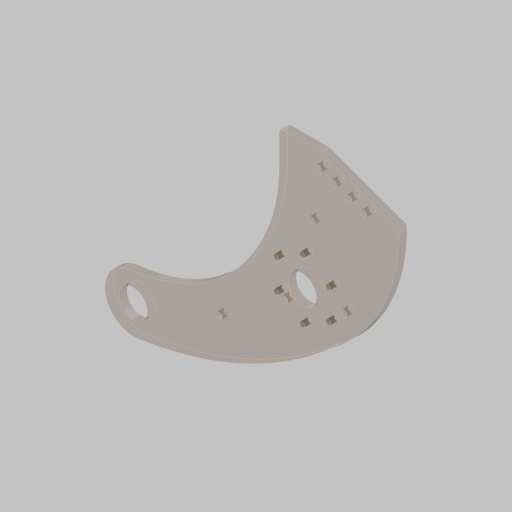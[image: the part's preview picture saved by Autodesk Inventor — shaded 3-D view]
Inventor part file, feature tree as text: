
AUTODESK INVENTOR PART (.ipt)
format: ipt  version: 2023.5 (Build 275446000, 446)  size: 253,440 bytes
history: native  units: in
note: dims shown in document units (in); Inventor stores cm internally (conversion verified against a paired STEP export)
features: sketch x5, hole x4, projected_geometry x3, extrude x2, fillet x2
ambient origin geometry x8: Origin, YZ Plane, XZ Plane, XY Plane, X Axis, Y Axis, Z Axis, Center Point
bodies: Solid1 (feature_tree)
feature tree (16):
  sketch  "Sketch1"  dims[d0=1.0in d1=3.0in]
  extrude  "Extrusion1"  Depth=3.0in
  hole  "Hole1"  [1 undecoded]
  hole  "Hole2"  [1 undecoded]
  fillet  "Fillet1"  Radius=0.5in
  hole  "Hole3"  [1 undecoded]
  hole  "Hole4"  [1 undecoded]
  extrude  "Extrusion2"  Depth=0.25in
  fillet  "Fillet2"  Radius=11.5in
  sketch  "Sketch5"  dims[d8=1.875in d9=0.875in]
  sketch  "Sketch3"  dims[d2=8.75in d3=5.75in]
  projected_geometry  "Projected Loop1"
  sketch  "Sketch4"  dims[d4=1.0in d5=3.0in d7=0.5in]
  projected_geometry  "Projected Loop2"
  sketch  "Sketch6"  dims[d10=1.9685in d12=0.5in d13=0.3937in d15=1.0in d17=0.5in d18=0.375in d19=11.5in d20=0.25in d21=0.0in d22=0.201in d23=0.38in d24=0.385in d25=0.25in d26=0.5635in d27=1.0in d28=0.8108in d29=0.875in d30=0.75in d31=0.507in d32=0.25in d33=0.5635in d34=1.0in d35=0.8108in d37=5.75in d38=2.5in d39=0.1374in d40=1.5748in d42=0.5in d43=0.3937in d45=1.0in d47=0.5in d48=0.125in d49=1.875in d50=2.3622in d52=360.0deg d54=0.156in d55=0.38in d56=0.385in d57=0.25in d58=0.5635in d59=1.0in d60=0.8108in d62=0.25in d63=0.25in d64=0.25in d65=0.25in d66=0.25in d67=0.25in d68=0.875in d69=0.875in d70=0.5in d71=0.125in d72=0.0in d73=0.13in d74=13.8531in d75=5.0044in d76=2.0in d77=2.0in d78=1.0in d79=1.0in d84=0.201in d85=0.75in d86=0.385in d87=0.25in d88=0.5635in d89=1.0in d90=0.8108in d91=10.25in d92=2.5in d93=1.0in]
  projected_geometry  "Projected Loop3"
note: 4 required parameter values undecoded (feature->parameter linkage not recoverable at this tier; creation-order binding heuristic only, values carry confidence <= 0.55)
